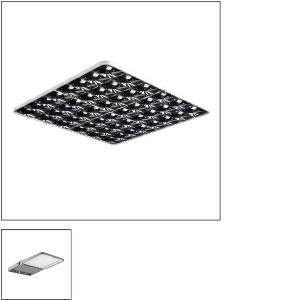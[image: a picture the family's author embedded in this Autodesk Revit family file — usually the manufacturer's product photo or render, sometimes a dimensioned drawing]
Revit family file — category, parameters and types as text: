
# Revit family: siteco_mirrortec_r__indoor___rs05_5nw14091qb_062b
name_source: partatom
category: Lighting Fixtures
units: mm (PartAtom-declared; Revit-internal decimal feet)

## family parameters
Cut with Voids When Loaded = No
Host = Face
Light Source = No
Part Type = Normal
Room Calculation Point = No
Round Connector Dimension = Use Diameter
Shared = No

## types (1)
- 5XA7682G2H2AC (1 x LED, 33820 lm, 305.7 W, 4000K)
    Apparent Load = 306 VA
    CIE Flux Codes = 47 83 98 55 100
    Color Rendering = 70
    Color Temperature = 4000K
    Default Elevation = 1800 mm
    Description = secondary reflector, for Siteco Mirrortec® Indoor, ball-and-socket joint pendant suspension, housing, square, of aluminium, coated, metallic grey (RAL 9006), fresnel reflector 100, of PMMA, aluminized, highly specular, light point resolution, fresnel structure, length: 900 mm, width: 900 mm

Light Distribution: RS05
    Height = 502 mm
    Lamp = 1 x LED
    Lamp Light Flux = 33820 lm
    Lamp Power = 305.7 W
    Lamp count = 1
    Length = 919 mm
    Luminous efficacy = 111 lm/W
    Manufacturer = Siteco
    ModVariant = No
    Model = 5NW14091QB
    Mounting Place = Ceiling
    Mounting Type = Pendant
    Number of Poles = 1
    OnlyDefault = Yes
    Power Factor = 1
    Product Name = Siteco Mirrortec® Indoor | RS05
    Product group = secondary reflector
    ProductGroupID = 910
    Protection Class = Protection class II
    Protection Degree = IP 66
    RLX_Detail_Level = 1
    RlxData = <blob elided: 104533 chars, md5=2054c5e3>
    Socket = socket
    Standby Power = 0 W
    System Light Flux = 33820 lm
    System Power = 306 W
    Type Comments = Floodlight FL 20 midi, floodlight, primary light control with lens, of plastic, primary optical cover: protective disc, of toughened safety glass, transparent, light distribution: RS05, light emission: direct distribution, primary light characteristic: rotationally symmetric, installation type: surface-mounted, LED High Power LED, rated luminous flux: 38.380 lm, light colour: 740, colour temperature: 4000K, control gear: ECG Plus, control: overheat protection, power reduction, digital communication interface, time-dependent luminous flux control, flexible luminous flux parameterisation, electronic power reduction, with terminal, 10-pole, max. 2.5mm², mains connection: 220..240V, AC, 50/60Hz, rated input power: 306W, LED unit, of diecast aluminium, powder-coated, Siteco® metallic grey (DB 702S), length: 731 mm, width: 450 mm, height: 76mm, housing frame, of diecast aluminium, powder-coated, Siteco® metallic grey (DB 702S), wall fastening, DALIprotection rating (complete): IP66, insulation class (complete): insulation class II (safety insulation), certification: CE, ENEC, VDE, protection symbol: D, permissible ambient temperature for indoor applications: -40..+40°C, permissible ambient temperature for outdoor applications: -40..+50°C, standard: DIN EN 12944, packaging unit: 1 piece

individual setting: distance floodlight mirror = 2,5m / reflector tilt = 5°
    Type Image = l_577132_1005944.jpg
    URL = http://relux.com
    VarID = 5xa7682g2h2ac@adj_128719
    Voltage = 0 V
    Weight = 0.00 kg
    Width = 919 mm

## geometry (parser evidence)
native form markers: Blend x4, Sweep x10
no freeform markers — native parametric forms only
